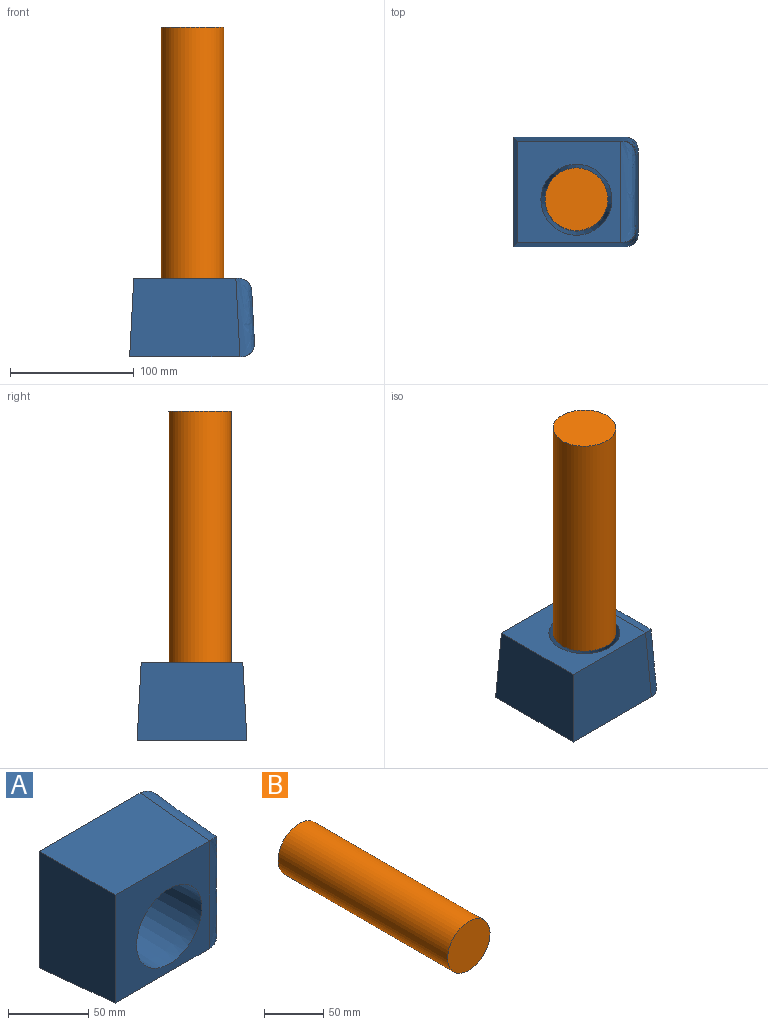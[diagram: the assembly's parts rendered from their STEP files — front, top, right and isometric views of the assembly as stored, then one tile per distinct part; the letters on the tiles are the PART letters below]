
ASSEMBLY  parts=2 mates=1
PART A: 11 faces, bbox 101.6x63.8x97.8 mm
  f0: plane 89.31x63.52mm, normal (0,-0.05,1), area 5466.4mm2, adj f1,f5,f6,f7,f8
  f1: plane 88.9x63.5mm, normal (-1,-0.05,0), area 5441.3mm2, adj f0,f2,f5,f6
  f2: plane 89.31x63.52mm, normal (0,-0.05,-1), area 5466.4mm2, adj f1,f5,f6,f7,f9
  f3: cone r=25.4mm half-angle=3deg, axis (0,-1,0), area 10812.9mm2, adj f5,f6
  f4: plane 62.93x38.86mm, normal (1,-0.05,0), area 2369.4mm2, adj f7,f8,f9,f10
  f5: plane 83.27x82.26mm, normal (0,-1,0), area 4252.9mm2, adj f0,f1,f2,f3,f8,f9,f10
  f6: plane 88.9x88.62mm, normal (0,1,0), area 5851.1mm2, adj f0,f1,f2,f3,f7
  f7: bspline ~97.79x12.98mm, area 1666.8mm2, adj f0,f2,f4,f6,f8,f9
  f8: bspline ~63.81x15.63mm, area 1102.2mm2, adj f0,f4,f5,f7,f10
  f9: bspline ~63.81x15.63mm, area 1102.2mm2, adj f2,f4,f5,f7,f10
  f10: bspline ~90.47x12.31mm, area 1357.5mm2, adj f4,f5,f8,f9
PART B: 3 faces, bbox 50.8x203.2x50.8 mm
  f0: cylinder r=25.4mm len=203.2mm, axis (0,-1,0), area 32429.3mm2, adj f1,f2
  f1: plane 50.8x50.8mm, normal (0,1,0), area 2026.8mm2, adj f0
  f2: plane 50.8x50.8mm, normal (0,-1,0), area 2026.8mm2, adj f0
PLACE A rot(axis=(-1,0,0),90deg) t=(0,101.6,-165.1)mm
PLACE B rot(axis=(-1,0,0),90deg) t=(0,101.6,-4.83)mm
MATE fastened A.f3 <-> B.f0  axis (0,0,1) through (0,101.6,-101.6)mm
